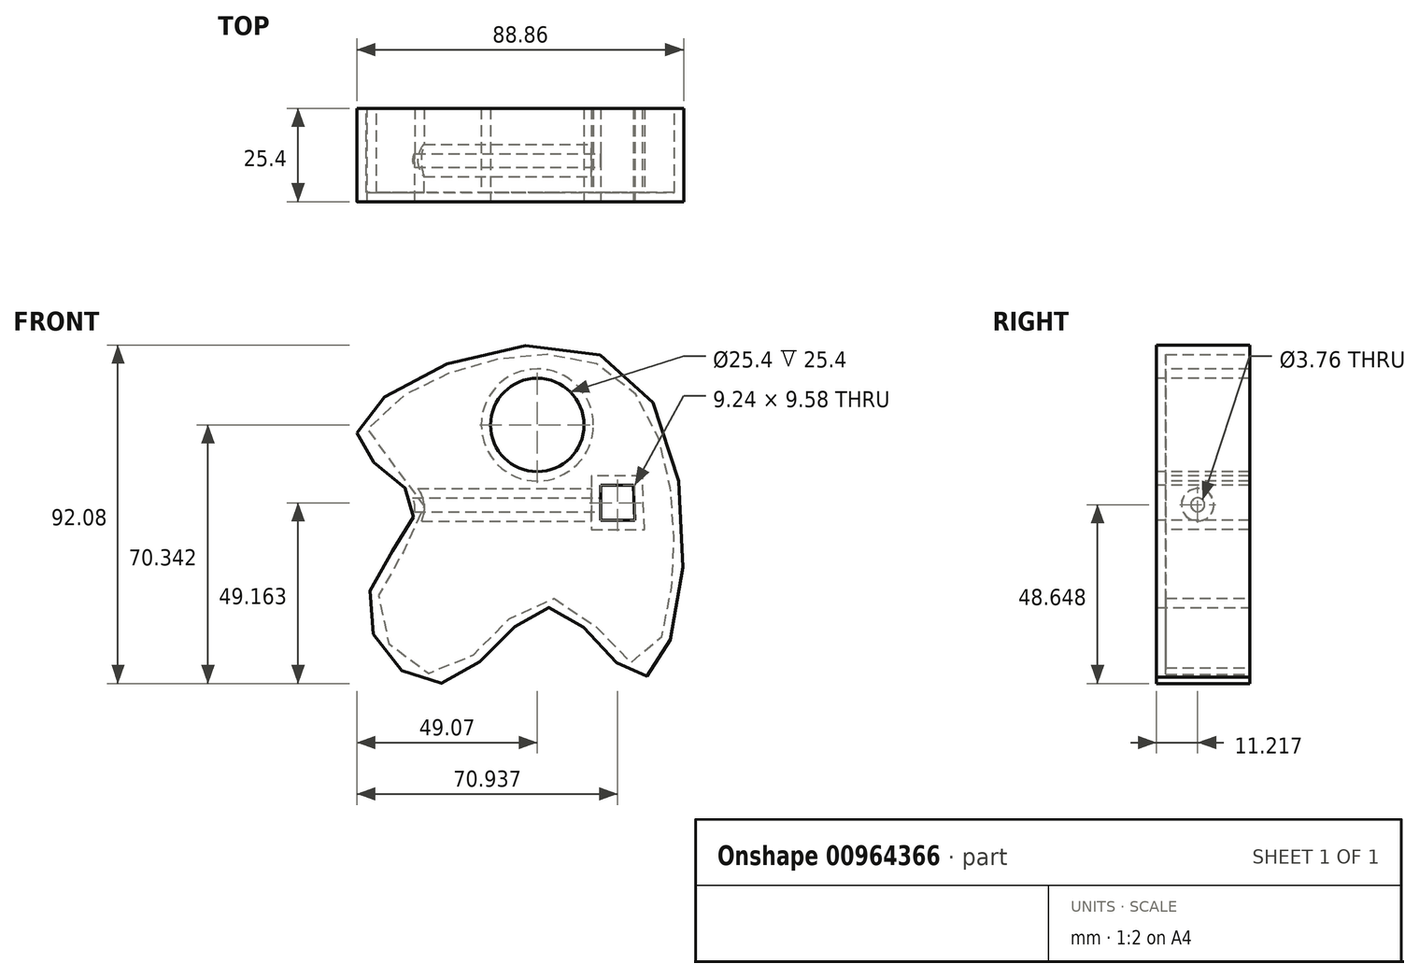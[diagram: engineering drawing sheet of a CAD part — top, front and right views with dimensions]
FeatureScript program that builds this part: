
annotation { "Feature Type Name" : "Feature", "Feature Type Description" : "" }
export const myFeature = defineFeature(function(context is Context, id is Id, definition is map)
    precondition{}
    {
        {
            var Q0;
            Q0=qCreatedBy(makeId("Front.planeOp"),FACE);
            var sketch = newSketch(context, id + "F0", { "sketchPlane" : qUnion([Q0])});
            skFitSpline(sketch, "E0", {"points": [v(-49.04, 40.58) * mm, v(-33.5, 21.87) * mm, v(-46.16, -5.76) * mm, v(-25.15, -27.35) * mm, v(4.21, -6.9) * mm, v(29.54, -25.62) * mm, v(23.5, 58.14) * mm, v(-49.04, 40.58) * mm]});
            skSolve(sketch);
        }
        {
            var Q0;
            Q0=makeQuery(id+"F0.imprint","IMPRINT",FACE,{"disambiguationData":[TD([[makeQuery(id+"F0.imprint","IMPRINT",EDGE,{"derivedFrom":sQuery(id+"F0.wireOp",EDGE,"E0")}),1.0]])]});
            extrude(context, id + "F1", {"entities" : qUnion([Q0]), "depth" : 25.4 * mm, "offsetDistance" : 25.4 * mm});
        }
        {
            var Q0;
            Q0=makeQuery(id+"F1.opExtrude","CAP_FACE",FACE,{"disambiguationData":[OSD([sQuery(id+"F0.wireOp",EDGE,"E0")])],"isStart":false});
            var sketch = newSketch(context, id + "F2", { "sketchPlane" : qUnion([Q0])});
            skCircle(sketch, "E1", {"center": v(0, 42.78) * mm, "radius": 12.7 * mm});
            skSolve(sketch);
        }
        {
            var Q0;
            Q0=sQuery(id+"F2.wireOp",VERTEX,"E1.center");
            var Q1;
            Q1=makeQuery(id+"F1.opExtrude","SWEPT_BODY",BODY,{"disambiguationData":[OSD([sQuery(id+"F0.wireOp",EDGE,"E0")])]});
            hole(context, id + "F3", {"style" : HoleStyle.SIMPLE, "endStyle" : HoleEndStyle.BLIND, "holeDiameter" : 25.4 * mm, "majorDiameter" : 6.35 * mm, "holeDepth" : 25.4 * mm, "isTappedThrough" : true, "tappedDepth" : 12.7 * mm, "tapClearance" : 3, "locations" : qUnion([Q0]), "scope" : qUnion([Q1])});
        }
        {
            var Q0;
            Q0=qCreatedBy(makeId("Front.planeOp"),FACE);
            var sketch = newSketch(context, id + "F4", { "sketchPlane" : qUnion([Q0])});
            skLineSegment(sketch, "E2", {"start": v(26.15, 26.4) * mm, "end": v(17.25, 26.4) * mm});
            skLineSegment(sketch, "E3", {"start": v(17.25, 26.4) * mm, "end": v(17.25, 16.81) * mm});
            skLineSegment(sketch, "E4", {"start": v(17.25, 16.81) * mm, "end": v(26.49, 16.81) * mm});
            skLineSegment(sketch, "E5", {"start": v(26.49, 16.81) * mm, "end": v(26.15, 26.4) * mm});
            skSolve(sketch);
        }
        {
            var Q0;
            Q0=makeQuery(id+"F4.imprint","IMPRINT",FACE,{"disambiguationData":[TD([[makeQuery(id+"F4.imprint","IMPRINT",EDGE,{"derivedFrom":sQuery(id+"F4.wireOp",EDGE,"E2")}),1.0]])]});
            extrude(context, id + "F5", {"entities" : qUnion([Q0]), "operationType" : NewBodyOperationType.ADD, "depth" : 41.15 * mm, "offsetDistance" : 25.4 * mm});
        }
        {
            var Q0;
            Q0=makeQuery(id+"F5.opExtrude","CAP_FACE",FACE,{"disambiguationData":[OSD([sQuery(id+"F4.wireOp",EDGE,"E2"),sQuery(id+"F4.wireOp",EDGE,"E3"),sQuery(id+"F4.wireOp",EDGE,"E4"),sQuery(id+"F4.wireOp",EDGE,"E5")])],"isStart":false});
            extrude(context, id + "F6", {"entities" : qUnion([Q0]), "operationType" : NewBodyOperationType.REMOVE, "endBound" : BoundingType.SYMMETRIC, "oppositeDirection" : true, "depth" : 193.55 * mm, "offsetDistance" : 25.4 * mm});
        }
        {
            var Q0;
            Q0=makeQuery(id+"F6.boolean.opBoolean","COPY",FACE,{"derivedFrom":makeQuery(id+"F6.opExtrude","SWEPT_FACE",FACE,{"disambiguationData":[OSD([sQuery(id+"F4.wireOp",EDGE,"E3")])]})});
            var sketch = newSketch(context, id + "F7", { "sketchPlane" : qUnion([Q0])});
            skCircle(sketch, "E6", {"center": v(-14.18, 21.09) * mm, "radius": 1.88 * mm});
            skSolve(sketch);
        }
        {
            var Q0;
            Q0=makeQuery(id+"F7.imprint","IMPRINT",FACE,{"disambiguationData":[TD([[makeQuery(id+"F7.imprint","IMPRINT",EDGE,{"derivedFrom":sQuery(id+"F7.wireOp",EDGE,"E6")}),1.0]])]});
            extrude(context, id + "F8", {"entities" : qUnion([Q0]), "operationType" : NewBodyOperationType.REMOVE, "oppositeDirection" : true, "depth" : 63.25 * mm, "offsetDistance" : 25.4 * mm});
        }
        {
            var Q0;
            Q0=makeQuery(id+"F1.opExtrude","CAP_FACE",FACE,{"disambiguationData":[OSD([sQuery(id+"F0.wireOp",EDGE,"E0")])],"isStart":true});
            shell(context, id + "F9", {"entities" : qUnion([Q0]), "thickness" : 2.54 * mm});
        }
    });
